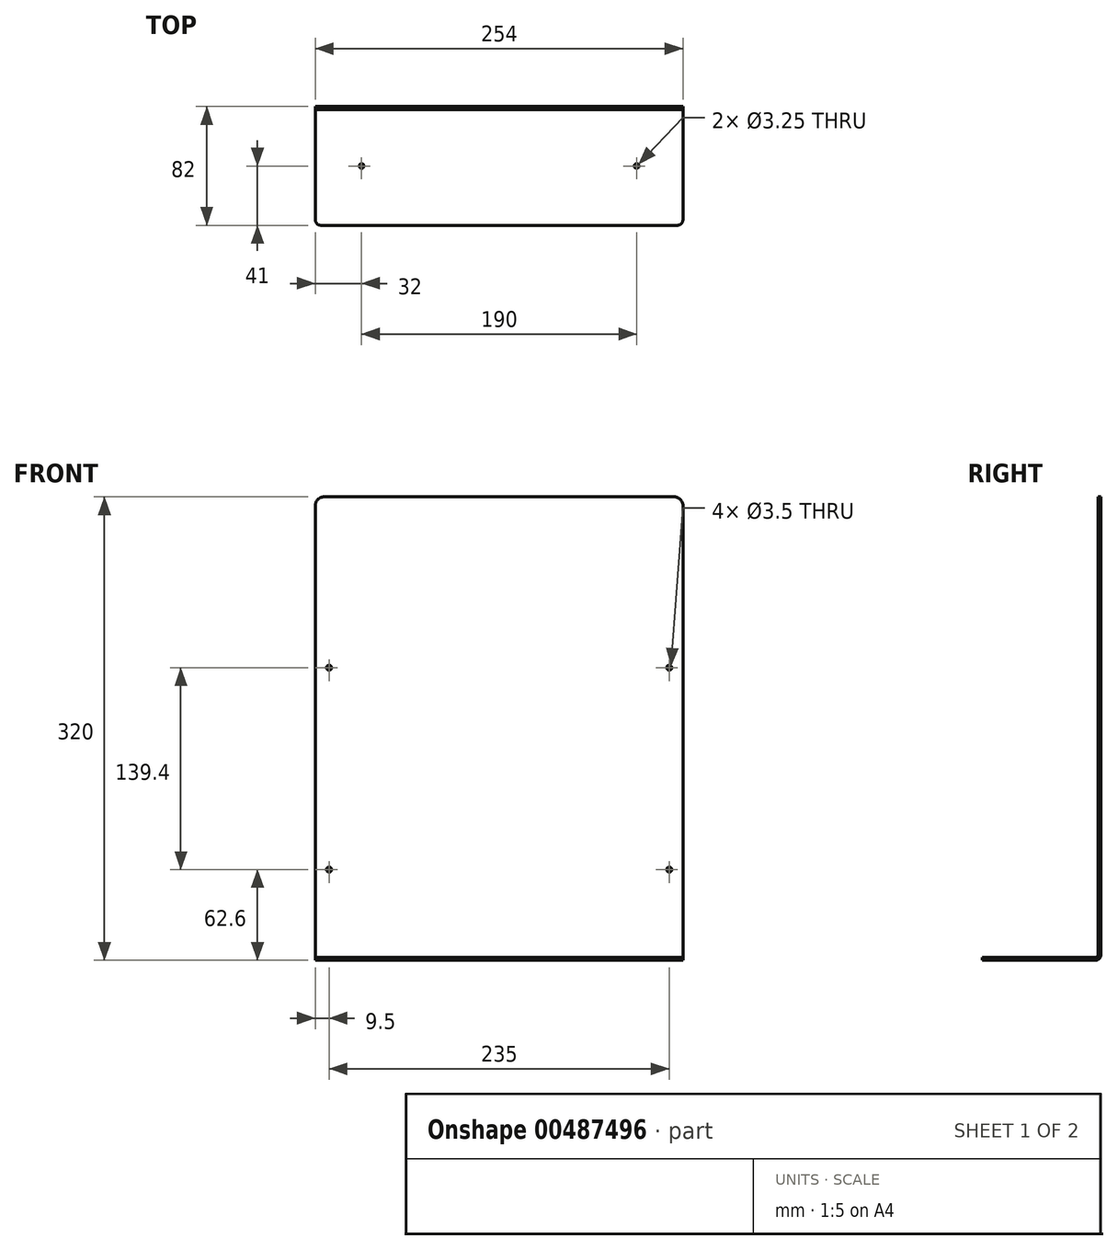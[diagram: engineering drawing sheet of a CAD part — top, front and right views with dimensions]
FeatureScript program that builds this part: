
annotation { "Feature Type Name" : "Feature", "Feature Type Description" : "" }
export const myFeature = defineFeature(function(context is Context, id is Id, definition is map)
    precondition{}
    {
        {
            var Q0;
            Q0=qCreatedBy(makeId("Right.planeOp"),FACE);
            var sketch = newSketch(context, id + "F0", { "sketchPlane" : qUnion([Q0])});
            skLineSegment(sketch, "E0", {"start": v(0, 0) * mm, "end": v(-82, 0) * mm});
            skLineSegment(sketch, "E1", {"start": v(0, 0) * mm, "end": v(0, 320) * mm});
            skPoint(sketch, "E2.visualSharp", {"position": v(0, 0) * mm});
            skLineSegment(sketch, "E3.0", {"start": v(-2, 2) * mm, "end": v(-2, 320) * mm});
            skLineSegment(sketch, "E3.1", {"start": v(-2, 2) * mm, "end": v(-82, 2) * mm});
            skPoint(sketch, "E4.visualSharp", {"position": v(-2, 2) * mm});
            skLineSegment(sketch, "E5", {"start": v(-2, 320) * mm, "end": v(0, 320) * mm});
            skLineSegment(sketch, "E6", {"start": v(-82, 2) * mm, "end": v(-82, 0) * mm});
            skSolve(sketch);
        }
        {
            var Q0;
            Q0 = qSketchRegion(id + "F0", true);
            extrude(context, id + "F1", {"entities" : qUnion([Q0]), "endBound" : BoundingType.SYMMETRIC, "depth" : 254 * mm});
        }
        {
            var Q0;
            Q0=makeQuery(id+"F1.opExtrude","SWEPT_EDGE",EDGE,{"disambiguationData":[OSD([sQuery(id+"F0.wireOp",EDGE,"E3.0"),sQuery(id+"F0.wireOp",EDGE,"E3.1")])]});
            fillet(context, id + "F2", {"entities" : qUnion([Q0]), "radius" : 2 * mm, "tangentPropagation" : true, "allowEdgeOverflow" : false});
        }
        {
            var Q0;
            Q0=makeQuery(id+"F1.opExtrude","SWEPT_EDGE",EDGE,{"disambiguationData":[OSD([sQuery(id+"F0.wireOp",EDGE,"E0"),sQuery(id+"F0.wireOp",EDGE,"E1")])]});
            fillet(context, id + "F3", {"entities" : qUnion([Q0]), "radius" : 4 * mm, "tangentPropagation" : true, "allowEdgeOverflow" : false});
        }
        {
            var Q0;
            Q0=makeQuery(id+"F1.opExtrude","CAP_EDGE",EDGE,{"disambiguationData":[OSD([sQuery(id+"F0.wireOp",EDGE,"E5")])],"isStart":false});
            var Q1;
            Q1=makeQuery(id+"F1.opExtrude","CAP_EDGE",EDGE,{"disambiguationData":[OSD([sQuery(id+"F0.wireOp",EDGE,"E5")])],"isStart":true});
            fillet(context, id + "F4", {"entities" : qUnion([Q0, Q1]), "radius" : 6 * mm, "tangentPropagation" : true, "allowEdgeOverflow" : false});
        }
        {
            var Q0;
            Q0=makeQuery(id+"F1.opExtrude","CAP_EDGE",EDGE,{"disambiguationData":[OSD([sQuery(id+"F0.wireOp",EDGE,"E6")])],"isStart":false});
            var Q1;
            Q1=makeQuery(id+"F1.opExtrude","CAP_EDGE",EDGE,{"disambiguationData":[OSD([sQuery(id+"F0.wireOp",EDGE,"E6")])],"isStart":true});
            fillet(context, id + "F5", {"entities" : qUnion([Q0, Q1]), "radius" : 4 * mm, "tangentPropagation" : true, "allowEdgeOverflow" : false});
        }
        {
            var Q0;
            Q0=makeQuery(id+"F1.opExtrude","SWEPT_FACE",FACE,{"disambiguationData":[OSD([sQuery(id+"F0.wireOp",EDGE,"E0")])]});
            var sketch = newSketch(context, id + "F6", { "sketchPlane" : qUnion([Q0])});
            skLineSegment(sketch, "E7", {"start": v(-95, 41) * mm, "end": v(95, 41) * mm, "construction": true});
            skCircle(sketch, "E8", {"center": v(95, 41) * mm, "radius": 1.62 * mm});
            skCircle(sketch, "E9", {"center": v(-95, 41) * mm, "radius": 1.62 * mm});
            skSolve(sketch);
        }
        {
            var Q0;
            Q0 = qSketchRegion(id + "F6", true);
            extrude(context, id + "F7", {"entities" : qUnion([Q0]), "operationType" : NewBodyOperationType.REMOVE, "endBound" : BoundingType.UP_TO_NEXT, "oppositeDirection" : true, "depth" : 25 * mm});
        }
        {
            var Q0;
            Q0=makeQuery(id+"F1.opExtrude","SWEPT_FACE",FACE,{"disambiguationData":[OSD([sQuery(id+"F0.wireOp",EDGE,"E1")])]});
            var sketch = newSketch(context, id + "F8", { "sketchPlane" : qUnion([Q0])});
            skLineSegment(sketch, "E10.bottom", {"start": v(-117.5, 202) * mm, "end": v(117.5, 202) * mm, "construction": true});
            skLineSegment(sketch, "E10.top", {"start": v(-117.5, 62.6) * mm, "end": v(117.5, 62.6) * mm, "construction": true});
            skLineSegment(sketch, "E10.left", {"start": v(-117.5, 202) * mm, "end": v(-117.5, 62.6) * mm, "construction": true});
            skLineSegment(sketch, "E10.right", {"start": v(117.5, 202) * mm, "end": v(117.5, 62.6) * mm, "construction": true});
            skCircle(sketch, "E11", {"center": v(117.5, 202) * mm, "radius": 1.75 * mm});
            skCircle(sketch, "E12", {"center": v(-117.5, 202) * mm, "radius": 1.75 * mm});
            skCircle(sketch, "E13", {"center": v(117.5, 62.6) * mm, "radius": 1.75 * mm});
            skCircle(sketch, "E14", {"center": v(-117.5, 62.6) * mm, "radius": 1.75 * mm});
            skSolve(sketch);
        }
        {
            var Q0;
            Q0 = qSketchRegion(id + "F8", true);
            var Q1;
            Q1=makeQuery(id+"F1.opExtrude","SWEPT_FACE",FACE,{"disambiguationData":[OSD([sQuery(id+"F0.wireOp",EDGE,"E3.0")])]});
            extrude(context, id + "F9", {"entities" : qUnion([Q0]), "operationType" : NewBodyOperationType.REMOVE, "endBound" : BoundingType.UP_TO_SURFACE, "oppositeDirection" : true, "endBoundEntityFace" : qUnion([Q1]), "depth" : 25 * mm});
        }
    });
